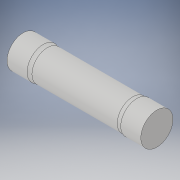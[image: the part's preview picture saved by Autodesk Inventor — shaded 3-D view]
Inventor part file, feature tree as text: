
AUTODESK INVENTOR PART (.ipt)
format: ipt  version: 2019 (Build 230136000, 136)  size: 114,688 bytes
history: native  units: in
note: dims shown in document units (in); Inventor stores cm internally (conversion verified against a paired STEP export)
features: fillet x2, revolve x1, sketch x1
ambient origin geometry x8: Origin, YZ Plane, XZ Plane, XY Plane, X Axis, Y Axis, Z Axis, Center Point
bodies: Solid1 (feature_tree)
feature tree (4):
  revolve  "Revolution1"  [1 undecoded]
  fillet  "Fillet1"  Radius=0.1181in
  fillet  "Fillet2"  Radius=0.0039in
  sketch  "Sketch1"  dims[d0=0.7874in d1=0.0945in d7=0.1181in d8=0.0039in d9=0.5512in d10=0.0039in d11=0.1181in d12=90.0deg d13=0.0787in d14=0.0787in]
note: 1 required parameter value undecoded (feature->parameter linkage not recoverable at this tier; creation-order binding heuristic only, values carry confidence <= 0.55)
